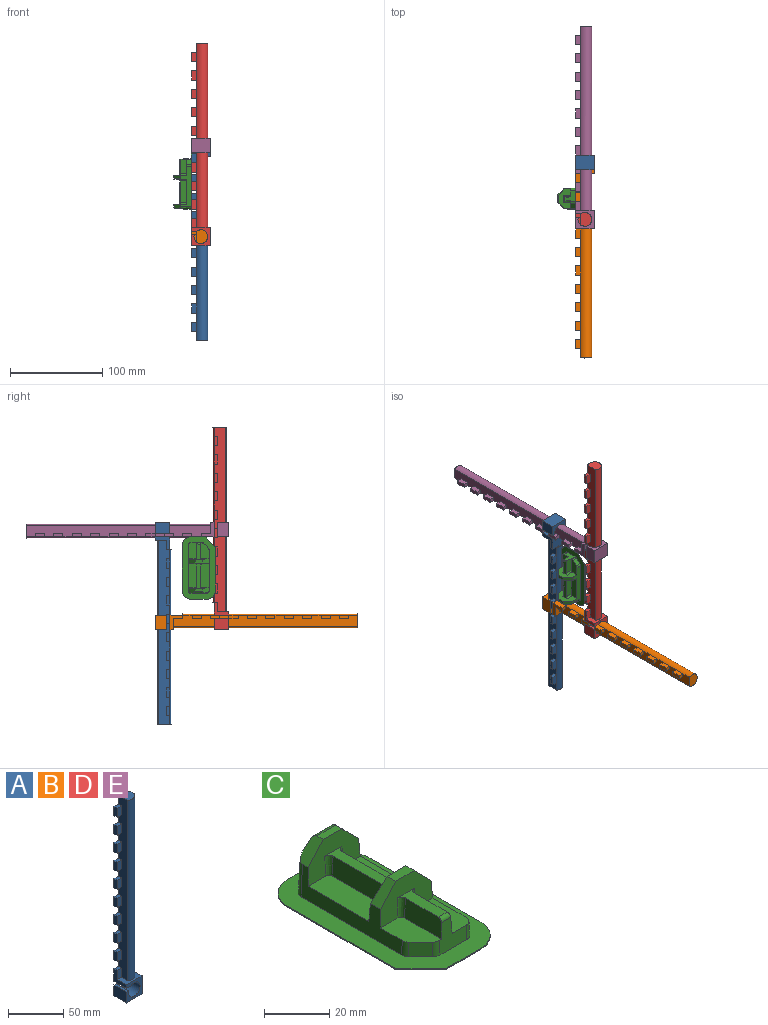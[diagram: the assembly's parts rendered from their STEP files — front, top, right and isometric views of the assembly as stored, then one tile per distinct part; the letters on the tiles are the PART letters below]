
ASSEMBLY  parts=5 mates=5
PART A: 61 faces, bbox 20x17.5x220 mm
  f0: plane 16x12mm, normal (-1,0,0), area 192mm2, adj f3,f6,f10,f58
  f1: plane 16x14mm, normal (-1,0,0), area 104mm2, adj f3,f5,f10,f11,f12,f59
  f2: cylinder r=7.5mm len=16mm, axis (0,1,0), area 675.1mm2, adj f3,f10,f58,f59
  f3: plane 20x20mm, normal (0,-1,0), area 208mm2, adj f0,f1,f2,f4,f5,f6,f58,f59
  f4: plane 20x16mm, normal (1,0,0), area 320mm2, adj f3,f5,f6,f10
  f5: plane 20x16mm, normal (0,0,1), area 155.6mm2, adj f1,f3,f4,f7,f9,f10,f12
  f6: plane 20x16mm, normal (0,0,-1), area 320mm2, adj f0,f3,f4,f10
  f7: cylinder r=7.5mm len=200mm, axis (0,0,-1), area 6546.4mm2, adj f5,f8,f9,f10,f14,f19,f24,f29
  f8: plane 15x12mm, normal (0,0,1), area 151.6mm2, adj f7,f9
  f9: plane 200x12mm, normal (-1,0,0), area 2000mm2, adj f5,f7,f8,f11,f12,f15,f16,f17
  f10: plane 30x20mm, normal (0,1,0), area 353mm2, adj f0,f1,f2,f4,f5,f6,f7,f11
  f11: plane 5.5x4mm, normal (0,0,1), area 22mm2, adj f1,f9,f10,f12
  f12: plane 10x5.5mm, normal (0,-1,0), area 55mm2, adj f1,f5,f9,f11
  f13: plane 10x4mm, normal (-1,0,0), area 40mm2, adj f14,f15,f16,f17
  f14: plane 10x5.5mm, normal (0,1,0), area 55mm2, adj f7,f13,f15,f16
  f15: plane 5.5x4mm, normal (0,0,-1), area 22mm2, adj f9,f13,f14,f17
  f16: plane 5.5x4mm, normal (0,0,1), area 22mm2, adj f9,f13,f14,f17
  f17: plane 10x5.5mm, normal (0,-1,0), area 55mm2, adj f9,f13,f15,f16
  f18: plane 10x4mm, normal (-1,0,0), area 40mm2, adj f19,f20,f21,f22
  f19: plane 10x5.5mm, normal (0,1,0), area 55mm2, adj f7,f18,f20,f21
  f20: plane 5.5x4mm, normal (0,0,-1), area 22mm2, adj f9,f18,f19,f22
  f21: plane 5.5x4mm, normal (0,0,1), area 22mm2, adj f9,f18,f19,f22
  f22: plane 10x5.5mm, normal (0,-1,0), area 55mm2, adj f9,f18,f20,f21
  f23: plane 10x4mm, normal (-1,0,0), area 40mm2, adj f24,f25,f26,f27
  f24: plane 10x5.5mm, normal (0,1,0), area 55mm2, adj f7,f23,f25,f26
  f25: plane 5.5x4mm, normal (0,0,-1), area 22mm2, adj f9,f23,f24,f27
  f26: plane 5.5x4mm, normal (0,0,1), area 22mm2, adj f9,f23,f24,f27
  f27: plane 10x5.5mm, normal (0,-1,0), area 55mm2, adj f9,f23,f25,f26
  f28: plane 10x4mm, normal (-1,0,0), area 40mm2, adj f29,f30,f31,f32
  f29: plane 10x5.5mm, normal (0,1,0), area 55mm2, adj f7,f28,f30,f31
  f30: plane 5.5x4mm, normal (0,0,-1), area 22mm2, adj f9,f28,f29,f32
  f31: plane 5.5x4mm, normal (0,0,1), area 22mm2, adj f9,f28,f29,f32
  f32: plane 10x5.5mm, normal (0,-1,0), area 55mm2, adj f9,f28,f30,f31
  f33: plane 10x4mm, normal (-1,0,0), area 40mm2, adj f34,f35,f36,f37
  f34: plane 10x5.5mm, normal (0,1,0), area 55mm2, adj f7,f33,f35,f36
  f35: plane 5.5x4mm, normal (0,0,-1), area 22mm2, adj f9,f33,f34,f37
  f36: plane 5.5x4mm, normal (0,0,1), area 22mm2, adj f9,f33,f34,f37
  f37: plane 10x5.5mm, normal (0,-1,0), area 55mm2, adj f9,f33,f35,f36
  f38: plane 10x4mm, normal (-1,0,0), area 40mm2, adj f39,f40,f41,f42
  f39: plane 10x5.5mm, normal (0,1,0), area 55mm2, adj f7,f38,f40,f41
  f40: plane 5.5x4mm, normal (0,0,-1), area 22mm2, adj f9,f38,f39,f42
  f41: plane 5.5x4mm, normal (0,0,1), area 22mm2, adj f9,f38,f39,f42
  f42: plane 10x5.5mm, normal (0,-1,0), area 55mm2, adj f9,f38,f40,f41
  f43: plane 10x4mm, normal (-1,0,0), area 40mm2, adj f44,f45,f46,f47
  f44: plane 10x5.5mm, normal (0,1,0), area 55mm2, adj f7,f43,f45,f46
  f45: plane 5.5x4mm, normal (0,0,-1), area 22mm2, adj f9,f43,f44,f47
  f46: plane 5.5x4mm, normal (0,0,1), area 22mm2, adj f9,f43,f44,f47
  f47: plane 10x5.5mm, normal (0,-1,0), area 55mm2, adj f9,f43,f45,f46
  f48: plane 10x4mm, normal (-1,0,0), area 40mm2, adj f49,f50,f51,f52
  f49: plane 10x5.5mm, normal (0,1,0), area 55mm2, adj f7,f48,f50,f51
  f50: plane 5.5x4mm, normal (0,0,-1), area 22mm2, adj f9,f48,f49,f52
  f51: plane 5.5x4mm, normal (0,0,1), area 22mm2, adj f9,f48,f49,f52
  f52: plane 10x5.5mm, normal (0,-1,0), area 55mm2, adj f9,f48,f50,f51
  f53: plane 10x4mm, normal (-1,0,0), area 40mm2, adj f54,f55,f56,f57
  f54: plane 10x5.5mm, normal (0,1,0), area 55mm2, adj f7,f53,f55,f56
  f55: plane 5.5x4mm, normal (0,0,-1), area 22mm2, adj f9,f53,f54,f57
  f56: plane 5.5x4mm, normal (0,0,1), area 22mm2, adj f9,f53,f54,f57
  f57: plane 10x5.5mm, normal (0,-1,0), area 55mm2, adj f9,f53,f55,f56
  f58: plane 16x2.77mm, normal (0,0,1), area 44.3mm2, adj f0,f2,f3,f10
  f59: plane 16x5.5mm, normal (0,0,-1), area 88mm2, adj f1,f2,f3,f10
  f60: plane 9x1.5mm, normal (0,0,-1), area 9.2mm2, adj f7,f10
PART B: same geometry as A
PART C: 86 faces, bbox 36.1x68.1x19.6 mm
  f0: plane 27.23x9.1mm, normal (0,0,-1), area 243.3mm2, adj f19,f30,f33,f48,f74,f75
  f1: plane 26.45x9.08mm, normal (0,0,1), area 237mm2, adj f3,f4,f16,f45,f52,f53
  f2: plane 26.45x9.08mm, normal (0,0,1), area 237mm2, adj f3,f4,f29,f47,f69,f73
  f3: plane 22.64x13.63mm, normal (0,1,0.05), area 198.5mm2, adj f1,f2,f14,f15,f16,f29,f46,f52
  f4: plane 22.64x13.63mm, normal (0,-1,0.05), area 198.5mm2, adj f1,f2,f16,f21,f22,f29,f46,f53
  f5: plane 17.62x9.13mm, normal (0,0,-1), area 155.7mm2, adj f19,f27,f34,f42,f59,f71
  f6: plane 22.64x13.63mm, normal (0,-1,0.05), area 198.5mm2, adj f7,f8,f14,f15,f16,f29,f39,f54
  f7: plane 17.57x9.08mm, normal (0,0,1), area 133.5mm2, adj f6,f16,f35,f36,f40,f54,f56,f58
  f8: plane 17.63x9.15mm, normal (0,0,1), area 155.5mm2, adj f6,f29,f36,f41,f60,f68
  f9: plane 10.12x10.12mm, normal (-0.71,-0.71,0), area 5.7mm2, adj f26,f37,f78,f82
  f10: plane 48x0.4mm, normal (1,0,0), area 19.2mm2, adj f26,f37,f83,f85
  f11: plane 46.53x0.4mm, normal (-1,0,0), area 18.6mm2, adj f26,f37,f82,f84
  f12: plane 14.73x0.4mm, normal (0,-1,0), area 5.9mm2, adj f26,f37,f78,f83
  f13: plane 17.58x9.1mm, normal (0,0,-1), area 134.8mm2, adj f20,f27,f28,f34,f44,f57,f67,f76
  f14: plane 6.92x6.92mm, normal (-0.71,0,0.71), area 39.7mm2, adj f3,f6,f16,f66
  f15: plane 6.92x6.92mm, normal (0.71,0,0.71), area 39.7mm2, adj f3,f6,f29,f66
  f16: plane 43.94x12.1mm, normal (-1,0,0.05), area 281.6mm2, adj f1,f3,f4,f6,f7,f14,f21,f37
  f17: plane 6.7x6.7mm, normal (-0.71,0,-0.71), area 34.4mm2, adj f19,f25,f30,f51,f64,f79
  f18: plane 6.7x6.7mm, normal (0.71,0,-0.71), area 34.4mm2, adj f20,f25,f30,f61,f64,f79
  f19: plane 49.09x12.33mm, normal (-1,0,-0.05), area 302.4mm2, adj f0,f5,f17,f26,f30,f32,f33,f34
  f20: plane 43.92x12.33mm, normal (1,0,-0.05), area 275.1mm2, adj f13,f18,f24,f26,f30,f31,f33,f34
  f21: plane 6.92x6.92mm, normal (-0.71,0,0.71), area 42.4mm2, adj f4,f16,f23,f65,f72,f81
  f22: plane 6.92x6.92mm, normal (0.71,0,0.71), area 42.4mm2, adj f4,f23,f29,f62,f65,f81
  f23: plane 17.54x17.31mm, normal (0,1,0.05), area 287.8mm2, adj f21,f22,f37,f62,f72,f81
  f24: plane 27.23x9.1mm, normal (0,0,-1), area 243.3mm2, adj f20,f30,f33,f50,f55,f70
  f25: plane 17.92x17.27mm, normal (0,-1,-0.05), area 290.3mm2, adj f17,f18,f26,f51,f61,f79
  f26: plane 68.13x36.13mm, normal (0,0,-1), area 1131.5mm2, adj f9,f10,f11,f12,f19,f20,f25,f27
  f27: plane 11.74x11.67mm, normal (0,1,-0.05), area 84.3mm2, adj f5,f13,f26,f42,f44,f59,f67,f77
  f28: plane 5.36x5.36mm, normal (0.71,0.71,-0.05), area 38.6mm2, adj f13,f26,f57,f67
  f29: plane 49.11x12.1mm, normal (1,0,0.05), area 308.9mm2, adj f2,f3,f4,f6,f8,f15,f22,f37
  f30: plane 21.89x13.63mm, normal (0,1,-0.05), area 191.1mm2, adj f0,f17,f18,f19,f20,f24,f49,f55
  f31: plane 6.7x6.7mm, normal (0.71,0,-0.71), area 31.1mm2, adj f20,f33,f34,f63
  f32: plane 6.7x6.7mm, normal (-0.71,0,-0.71), area 31.1mm2, adj f19,f33,f34,f63
  f33: plane 21.89x13.63mm, normal (0,-1,-0.05), area 191.1mm2, adj f0,f19,f20,f24,f31,f32,f49,f63
  f34: plane 21.89x13.63mm, normal (0,1,-0.05), area 191.1mm2, adj f5,f13,f19,f20,f31,f32,f43,f63
  f35: plane 5.36x5.36mm, normal (-0.71,-0.71,0.05), area 38.6mm2, adj f7,f37,f56,f58
  f36: plane 11.74x11.3mm, normal (0,-1,0.05), area 87.7mm2, adj f7,f8,f37,f40,f41,f58,f60,f80
  f37: plane 68.15x36.15mm, normal (0,0,1), area 1075.6mm2, adj f9,f10,f11,f12,f16,f23,f29,f35
  f38: plane 16x0.4mm, normal (0,1,0), area 6.4mm2, adj f26,f37,f84,f85
  f39: plane 16.26x7.58mm, normal (0,0,1), area 63.7mm2, adj f6,f40,f41,f54,f68,f80
  f40: plane 16.16x7.39mm, normal (-1,0,0.05), area 115.7mm2, adj f7,f36,f39,f54,f80
  f41: plane 16.16x7.39mm, normal (1,0,0.05), area 115.7mm2, adj f8,f36,f39,f68,f80
  f42: plane 15.77x7.38mm, normal (-1,0,-0.05), area 113.1mm2, adj f5,f27,f43,f71,f77
  f43: plane 16.65x7.6mm, normal (0,0,-1), area 53.2mm2, adj f34,f42,f44,f71,f76,f77
  f44: plane 15.77x7.38mm, normal (1,0,-0.05), area 113.1mm2, adj f13,f27,f43,f76,f77
  f45: plane 23.65x7.36mm, normal (-1,0,0.05), area 171.9mm2, adj f1,f46,f52,f53
  f46: plane 27.24x7.58mm, normal (0,0,1), area 107.4mm2, adj f3,f4,f45,f47,f52,f53,f69,f73
  f47: plane 23.65x7.36mm, normal (1,0,0.05), area 171.9mm2, adj f2,f46,f69,f73
  f48: plane 23.65x7.36mm, normal (-1,0,-0.05), area 171.9mm2, adj f0,f49,f74,f75
  f49: plane 28.01x7.6mm, normal (0,0,-1), area 90.4mm2, adj f30,f33,f48,f50,f55,f70,f74,f75
  f50: plane 23.65x7.36mm, normal (1,0,-0.05), area 171.9mm2, adj f24,f49,f55,f70
  f51: bspline ~16.18x3.03mm, area 49.1mm2, adj f17,f19,f25,f26
  f52: bspline ~8.26x1.95mm, area 18.7mm2, adj f1,f3,f45,f46
  f53: bspline ~8.26x1.95mm, area 18.7mm2, adj f1,f4,f45,f46
  f54: bspline ~8.26x1.95mm, area 18.7mm2, adj f6,f7,f39,f40
  f55: bspline ~8.3x2.33mm, area 23mm2, adj f24,f30,f49,f50
  f56: bspline ~5.92x2.3mm, area 12.7mm2, adj f7,f16,f35,f37
  f57: bspline ~5.31x2mm, area 11.2mm2, adj f13,f20,f26,f28
  f58: bspline ~5.92x2.3mm, area 12.7mm2, adj f7,f35,f36,f37
  f59: bspline ~6.15x2.91mm, area 22.2mm2, adj f5,f19,f26,f27
  f60: bspline ~5.36x3.21mm, area 25.4mm2, adj f8,f29,f36,f37
  f61: bspline ~14.42x2.86mm, area 49.1mm2, adj f18,f20,f25,f26
  f62: bspline ~16.4x3.41mm, area 56.2mm2, adj f22,f23,f29,f37
  f63: plane 7.77x2.93mm, normal (0,0,-1), area 22.8mm2, adj f31,f32,f33,f34
  f64: plane 7.77x2.42mm, normal (0,0,-1), area 18.8mm2, adj f17,f18,f30,f79
  f65: plane 8.1x2.8mm, normal (0,0,1), area 22.6mm2, adj f4,f21,f22,f81
  f66: plane 8.1x3.69mm, normal (0,0,1), area 29.9mm2, adj f3,f6,f14,f15
  f67: bspline ~5.31x2mm, area 11.2mm2, adj f13,f26,f27,f28
  f68: bspline ~8.26x1.95mm, area 18.7mm2, adj f6,f8,f39,f41
  f69: bspline ~8.26x1.95mm, area 18.7mm2, adj f2,f4,f46,f47
  f70: bspline ~8.3x2.33mm, area 23mm2, adj f24,f33,f49,f50
  f71: bspline ~8.3x2.33mm, area 23mm2, adj f5,f34,f42,f43
  f72: bspline ~16.4x3.41mm, area 56.2mm2, adj f16,f21,f23,f37
  f73: bspline ~8.26x1.95mm, area 18.7mm2, adj f2,f3,f46,f47
  f74: bspline ~8.3x2.33mm, area 23mm2, adj f0,f33,f48,f49
  f75: bspline ~8.3x2.33mm, area 23mm2, adj f0,f30,f48,f49
  f76: bspline ~8.3x2.33mm, area 23mm2, adj f13,f34,f43,f44
  f77: cylinder r=1mm len=3.19mm, axis (1,0,0), area 4.8mm2, adj f27,f42,f43,f44
  f78: cylinder r=1mm len=0.71mm, axis (0,0,-1), area 0.3mm2, adj f9,f12,f26,f37
  f79: cylinder r=1.1mm len=9.85mm, axis (-1,0,0), area 14.2mm2, adj f17,f18,f25,f64
  f80: cylinder r=1.4mm len=3.99mm, axis (1,0,0), area 8.3mm2, adj f36,f39,f40,f41
  f81: cylinder r=1.5mm len=10.94mm, axis (-1,0,0), area 20.8mm2, adj f21,f22,f23,f65
  f82: cylinder r=1.5mm len=1.06mm, axis (0,0,-1), area 0.5mm2, adj f9,f11,f26,f37
  f83: cylinder r=10mm len=10mm, axis (0,0,1), area 6.3mm2, adj f10,f12,f26,f37
  f84: cylinder r=10mm len=10mm, axis (0,0,1), area 6.3mm2, adj f11,f26,f37,f38
  f85: cylinder r=10mm len=10mm, axis (0,0,-1), area 6.3mm2, adj f10,f26,f37,f38
PART D: same geometry as A
PART E: same geometry as A
PLACE A rot(axis=(1,0,0),180deg) t=(-38.27,165.36,103.31)mm
PLACE B rot(axis=(1,0,0),90deg) t=(-38.27,175.36,16.29)mm fixed
PLACE C rot(axis=(-0.58,-0.58,0.58),120deg) t=(-48.67,138.11,63.49)mm
PLACE D t=(-38.27,125.49,6.29)mm
PLACE E rot(axis=(-1,0,0),90deg) t=(-38.27,115.49,93.31)mm
MATE slider E.f2 <-> D.f7  axis (0,0,1) through (-38.27,115.49,113.31)mm
MATE slider E.f7 <-> A.f2  axis (0,-1,0) through (-38.27,225.49,103.31)mm
MATE slider A.f7 <-> B.f2  axis (0,0,1) through (-38.27,175.36,-6.69)mm
MATE slider B.f7 <-> D.f2  axis (0,1,0) through (-38.27,65.36,6.29)mm
MATE planar C.f26 <-> B.f0  axis (1,0,0) through (-48.27,120.11,62.75)mm
